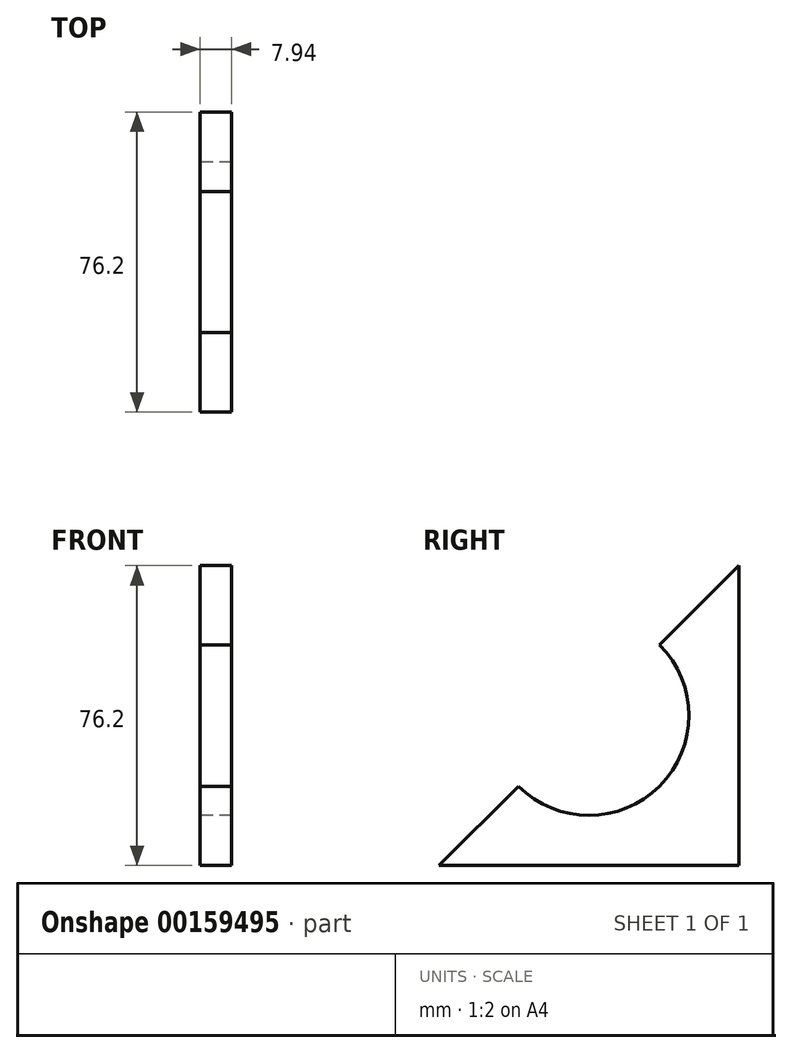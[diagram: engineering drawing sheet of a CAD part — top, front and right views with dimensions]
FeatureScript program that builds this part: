
annotation { "Feature Type Name" : "Feature", "Feature Type Description" : "" }
export const myFeature = defineFeature(function(context is Context, id is Id, definition is map)
    precondition{}
    {
        {
            var Q0;
            Q0=qCreatedBy(makeId("Right.planeOp"),FACE);
            var sketch = newSketch(context, id + "F0", { "sketchPlane" : qUnion([Q0])});
            skLineSegment(sketch, "E0.top", {"start": v(-83.88, -90.54) * mm, "end": v(-7.68, -90.54) * mm});
            skLineSegment(sketch, "E0.right", {"start": v(-7.68, -14.34) * mm, "end": v(-7.68, -90.54) * mm});
            skLineSegment(sketch, "E1", {"start": v(-83.88, -90.54) * mm, "end": v(-63.74, -70.4) * mm});
            skArc(sketch, "E2", {"start": v(-63.74, -70.4) * mm, "mid": v(-27.82, -70.4) * mm, "end": v(-27.82, -34.48) * mm});
            skLineSegment(sketch, "E3.trimOffspring", {"start": v(-27.82, -34.48) * mm, "end": v(-7.68, -14.34) * mm});
            skSolve(sketch);
        }
        {
            var Q0;
            Q0=makeQuery(id+"F0.imprint","IMPRINT",FACE,{"disambiguationData":[TD([[makeQuery(id+"F0.imprint","IMPRINT",EDGE,{"derivedFrom":sQuery(id+"F0.wireOp",EDGE,"E0.top")}),1.0]])]});
            extrude(context, id + "F1", {"entities" : qUnion([Q0]), "depth" : 7.94 * mm});
        }
    });
